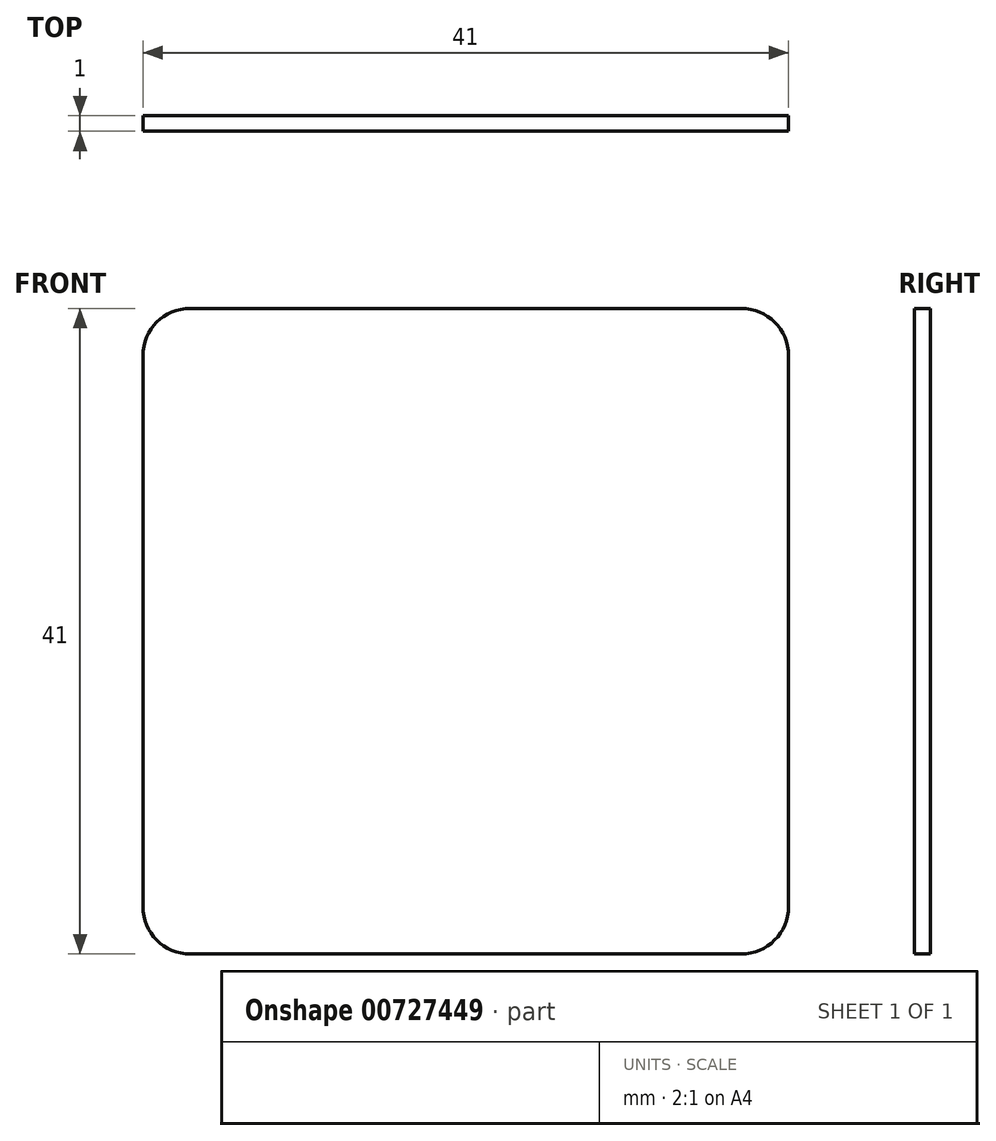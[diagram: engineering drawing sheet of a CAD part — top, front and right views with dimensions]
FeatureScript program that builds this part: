
annotation { "Feature Type Name" : "Feature", "Feature Type Description" : "" }
export const myFeature = defineFeature(function(context is Context, id is Id, definition is map)
    precondition{}
    {
        {
            var Q0;
            Q0=qCreatedBy(makeId("Front.planeOp"),FACE);
            var sketch = newSketch(context, id + "F0", { "sketchPlane" : qUnion([Q0])});
            skLineSegment(sketch, "E0.bottom", {"start": v(17.5, -20.5) * mm, "end": v(-17.5, -20.5) * mm});
            skLineSegment(sketch, "E0.top", {"start": v(17.5, 20.5) * mm, "end": v(-17.5, 20.5) * mm});
            skLineSegment(sketch, "E0.left", {"start": v(20.5, -17.5) * mm, "end": v(20.5, 17.5) * mm});
            skLineSegment(sketch, "E0.right", {"start": v(-20.5, -17.5) * mm, "end": v(-20.5, 17.5) * mm});
            skPoint(sketch, "E0.middle", {"position": v(0, 0) * mm});
            skPoint(sketch, "E1.visualSharp", {"position": v(-20.5, 20.5) * mm});
            skArc(sketch, "E1.filletArc", {"start": v(-17.5, 20.5) * mm, "mid": v(-19.62, 19.62) * mm, "end": v(-20.5, 17.5) * mm});
            skPoint(sketch, "E2.visualSharp", {"position": v(20.5, 20.5) * mm});
            skArc(sketch, "E2.filletArc", {"start": v(20.5, 17.5) * mm, "mid": v(19.62, 19.62) * mm, "end": v(17.5, 20.5) * mm});
            skPoint(sketch, "E3.visualSharp", {"position": v(20.5, -20.5) * mm});
            skArc(sketch, "E3.filletArc", {"start": v(17.5, -20.5) * mm, "mid": v(19.62, -19.62) * mm, "end": v(20.5, -17.5) * mm});
            skPoint(sketch, "E4.visualSharp", {"position": v(-20.5, -20.5) * mm});
            skArc(sketch, "E4.filletArc", {"start": v(-20.5, -17.5) * mm, "mid": v(-19.62, -19.62) * mm, "end": v(-17.5, -20.5) * mm});
            skSolve(sketch);
        }
        {
            var Q0;
            Q0 = qSketchRegion(id + "F0", true);
            extrude(context, id + "F1", {"entities" : qUnion([Q0]), "depth" : 1 * mm, "offsetDistance" : 25 * mm});
        }
        {
            var Q0;
            Q0=makeQuery(id+"F1.opExtrude","SWEPT_BODY",BODY,{"disambiguationData":[OSD([sQuery(id+"F0.wireOp",EDGE,"E0.bottom"),sQuery(id+"F0.wireOp",EDGE,"E0.top"),sQuery(id+"F0.wireOp",EDGE,"E0.left"),sQuery(id+"F0.wireOp",EDGE,"E0.right"),sQuery(id+"F0.wireOp",EDGE,"E1.filletArc"),sQuery(id+"F0.wireOp",EDGE,"E2.filletArc"),sQuery(id+"F0.wireOp",EDGE,"E3.filletArc"),sQuery(id+"F0.wireOp",EDGE,"E4.filletArc")])]});
            transform(context, id + "F2", {"entities" : qUnion([Q0]), "transformType" : TransformType.TRANSLATION_3D, "dx" : 0 * mm, "dy" : 0 * mm, "dz" : 0 * mm, "makeCopy" : true});
        }
    });
